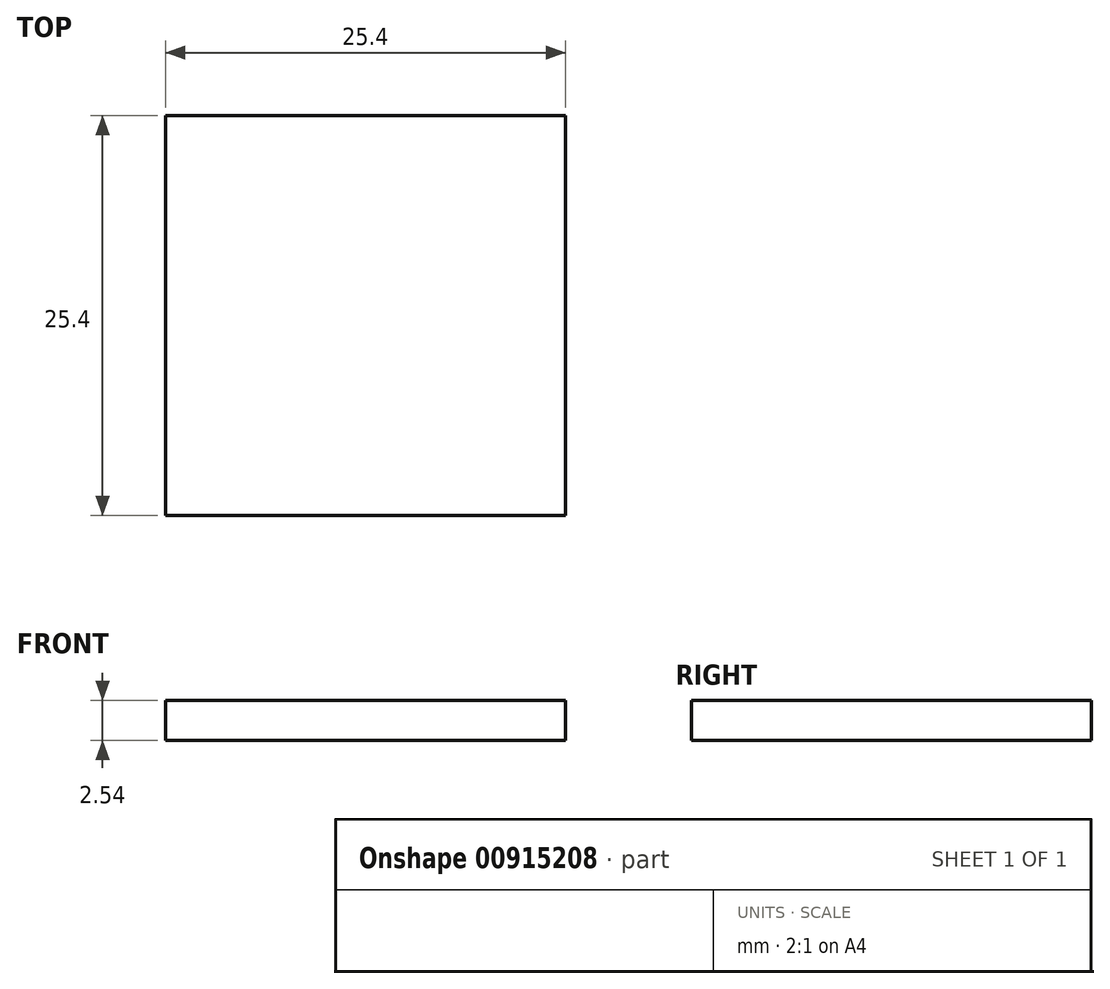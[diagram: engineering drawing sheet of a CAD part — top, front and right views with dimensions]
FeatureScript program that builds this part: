
annotation { "Feature Type Name" : "Feature", "Feature Type Description" : "" }
export const myFeature = defineFeature(function(context is Context, id is Id, definition is map)
    precondition{}
    {
        {
            var Q0;
            Q0=qCreatedBy(makeId("Top.planeOp"),FACE);
            var sketch = newSketch(context, id + "F0", { "sketchPlane" : qUnion([Q0])});
            skLineSegment(sketch, "E0.bottom", {"start": v(-6.3, 19.34) * mm, "end": v(19.1, 19.34) * mm});
            skLineSegment(sketch, "E0.top", {"start": v(-6.3, -6.06) * mm, "end": v(19.1, -6.06) * mm});
            skLineSegment(sketch, "E0.left", {"start": v(-6.3, 19.34) * mm, "end": v(-6.3, -6.06) * mm});
            skLineSegment(sketch, "E0.right", {"start": v(19.1, 19.34) * mm, "end": v(19.1, -6.06) * mm});
            skSolve(sketch);
        }
        {
            var Q0;
            Q0=makeQuery(id+"F0.imprint","IMPRINT",FACE,{"disambiguationData":[TD([[makeQuery(id+"F0.imprint","IMPRINT",EDGE,{"derivedFrom":sQuery(id+"F0.wireOp",EDGE,"E0.bottom")}),-1.0]])]});
            extrude(context, id + "F1", {"entities" : qUnion([Q0]), "depth" : 2.54 * mm, "offsetDistance" : 25.4 * mm});
        }
    });
